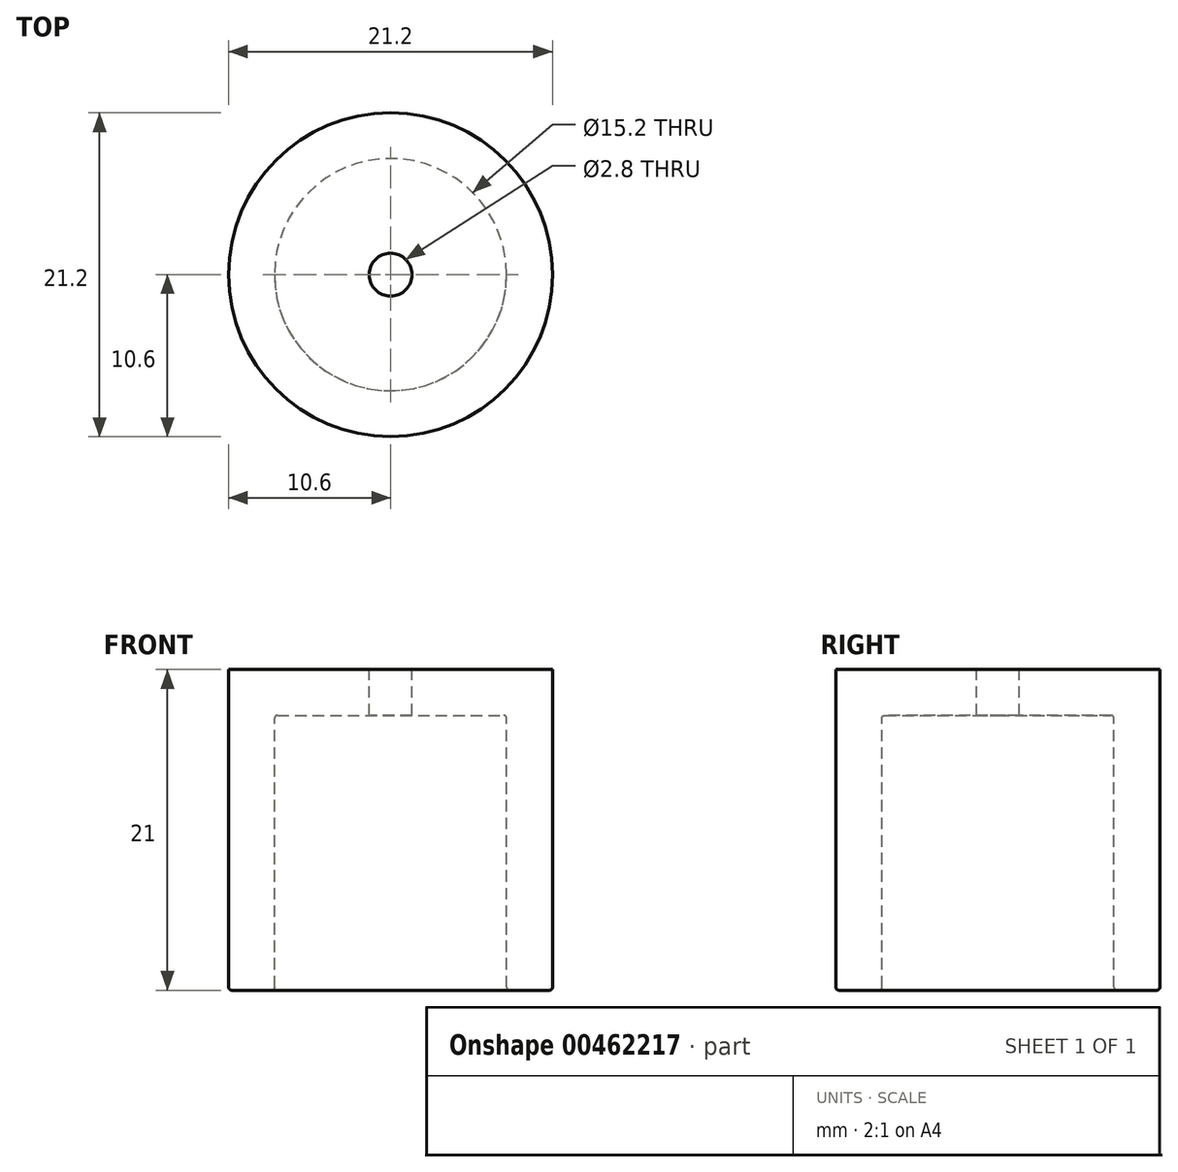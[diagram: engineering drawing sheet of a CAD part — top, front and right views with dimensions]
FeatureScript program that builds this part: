
annotation { "Feature Type Name" : "Feature", "Feature Type Description" : "" }
export const myFeature = defineFeature(function(context is Context, id is Id, definition is map)
    precondition{}
    {
        {
            var Q0;
            Q0=qCreatedBy(makeId("Front.planeOp"),FACE);
            var sketch = newSketch(context, id + "F0", { "sketchPlane" : qUnion([Q0])});
            skLineSegment(sketch, "E0", {"start": v(7.6, 18) * mm, "end": v(7.6, 0) * mm});
            skLineSegment(sketch, "E1", {"start": v(7.6, 0) * mm, "end": v(10.6, 0) * mm});
            skLineSegment(sketch, "E2", {"start": v(10.6, 0) * mm, "end": v(10.6, 21) * mm});
            skLineSegment(sketch, "E3", {"start": v(7.6, 18) * mm, "end": v(1.4, 18) * mm});
            skLineSegment(sketch, "E4", {"start": v(1.4, 18) * mm, "end": v(1.4, 21) * mm});
            skLineSegment(sketch, "E5", {"start": v(1.4, 21) * mm, "end": v(10.6, 21) * mm});
            skLineSegment(sketch, "E6", {"start": v(0, 21) * mm, "end": v(0, 17.66) * mm});
            skSolve(sketch);
        }
        {
            var Q0;
            Q0=makeQuery(id+"F0.imprint","IMPRINT",FACE,{"disambiguationData":[TD([[makeQuery(id+"F0.imprint","IMPRINT",EDGE,{"derivedFrom":sQuery(id+"F0.wireOp",EDGE,"E0")}),1.0]])]});
            var Q1;
            Q1=sQuery(id+"F0.wireOp",EDGE,"E6");
            revolve(context, id + "F1", {"entities" : qUnion([Q0]), "axis" : qUnion([Q1]), "revolveType" : RevolveType.FULL});
        }
        {
            var Q0;
            Q0=makeQuery(id+"F1.opRevolve","SWEPT_EDGE",EDGE,{"disambiguationData":[OSD([sQuery(id+"F0.wireOp",EDGE,"Xie8FKQn-zevv-FlhB-Fmwl-EtOxSmUnmpF7"),sQuery(id+"F0.wireOp",EDGE,"E0")])]});
            var Q1;
            Q1=makeQuery(id+"F1.opRevolve","SWEPT_EDGE",EDGE,{"disambiguationData":[OSD([sQuery(id+"F0.wireOp",EDGE,"E0"),sQuery(id+"F0.wireOp",EDGE,"E1")])]});
            var Q2;
            Q2=makeQuery(id+"F1.opRevolve","SWEPT_EDGE",EDGE,{"disambiguationData":[OSD([sQuery(id+"F0.wireOp",EDGE,"E1"),sQuery(id+"F0.wireOp",EDGE,"E2")])]});
            fillet(context, id + "F2", {"entities" : qUnion([Q0, Q1, Q2]), "radius" : .2 * mm, "tangentPropagation" : true, "allowEdgeOverflow" : false});
        }
    });
